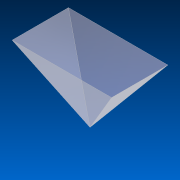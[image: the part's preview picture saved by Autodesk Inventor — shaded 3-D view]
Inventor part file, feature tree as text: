
AUTODESK INVENTOR PART (.ipt)
format: ipt  version: 2021.1 (Build 251245010, 245A)  size: 98,816 bytes
history: native  units: in
note: dims shown in document units (in); Inventor stores cm internally (conversion verified against a paired STEP export)
features: sketch x3, extrude x3, plane x1, shell x1
ambient origin geometry x8: Origin, YZ Plane, XZ Plane, XY Plane, X Axis, Y Axis, Z Axis, Center Point
bodies: Solid1 (feature_tree)
feature tree (8):
  sketch  "Sketch2"  dims[d0=0.323in d1=75.0deg]
  sketch  "Sketch3"  dims[d2=15.0in d3=15.0in d4=15.0in]
  plane  "Work Plane1"
  extrude  "Extrusion1"  TaperAngle=75.0deg  [1 undecoded]
  extrude  "Extrusion2"  Depth=15.0in
  extrude  "Extrusion3"  TaperAngle=0.0deg  [1 undecoded]
  shell  "Shell1"  Thickness=0.0in
  sketch  "Sketch4"  dims[d5=1.0in d6=0.0in d7=0.0in d8=0.0in d9=0.0in d10=0.0in d11=0.0001in]
note: 2 required parameter values undecoded (feature->parameter linkage not recoverable at this tier; creation-order binding heuristic only, values carry confidence <= 0.55)
